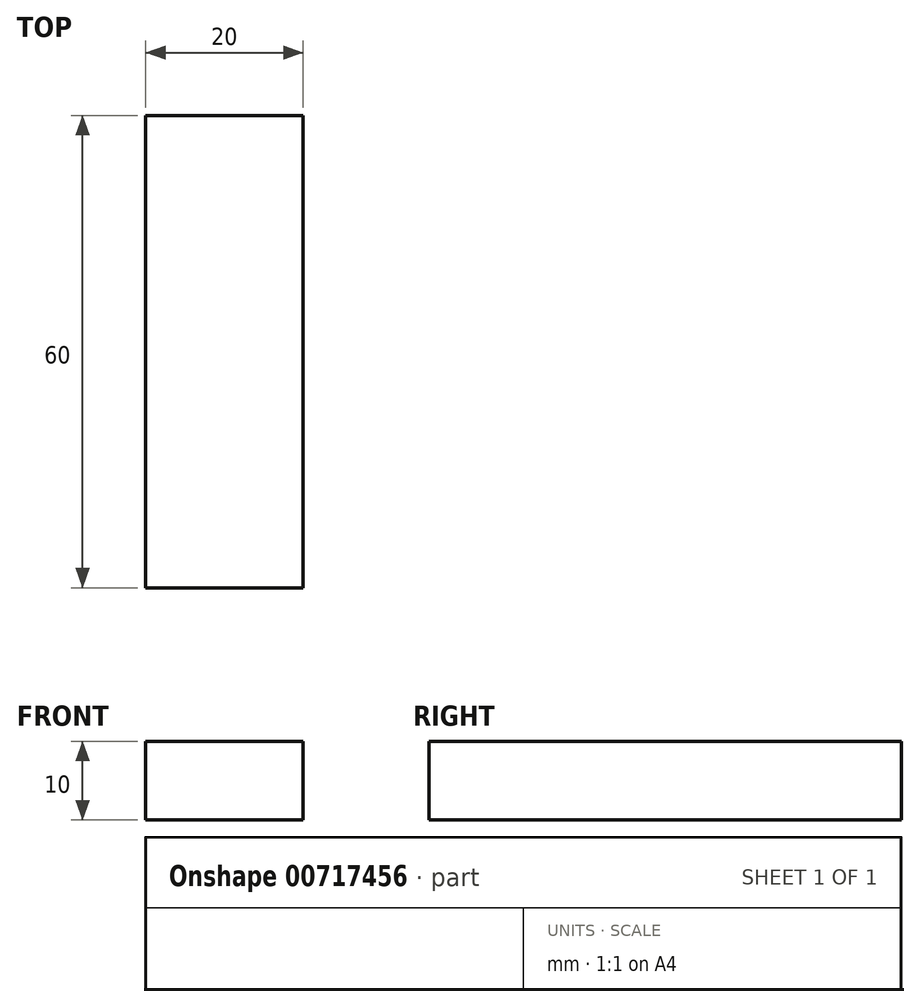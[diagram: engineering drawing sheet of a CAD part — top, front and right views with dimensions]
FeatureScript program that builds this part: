
annotation { "Feature Type Name" : "Feature", "Feature Type Description" : "" }
export const myFeature = defineFeature(function(context is Context, id is Id, definition is map)
    precondition{}
    {
        {
            var Q0;
            Q0=qCreatedBy(makeId("Front.planeOp"),FACE);
            var sketch = newSketch(context, id + "F0", { "sketchPlane" : qUnion([Q0])});
            skLineSegment(sketch, "E0.bottom", {"start": v(-55.41, 67.44) * mm, "end": v(-35.41, 67.44) * mm});
            skLineSegment(sketch, "E0.top", {"start": v(-55.41, 57.44) * mm, "end": v(-35.41, 57.44) * mm});
            skLineSegment(sketch, "E0.left", {"start": v(-55.41, 67.44) * mm, "end": v(-55.41, 57.44) * mm});
            skLineSegment(sketch, "E0.right", {"start": v(-35.41, 67.44) * mm, "end": v(-35.41, 57.44) * mm});
            skSolve(sketch);
        }
        {
            var Q0;
            Q0 = qSketchRegion(id + "F0", true);
            extrude(context, id + "F1", {"entities" : qUnion([Q0]), "depth" : 60 * mm, "offsetDistance" : 25 * mm});
        }
    });
